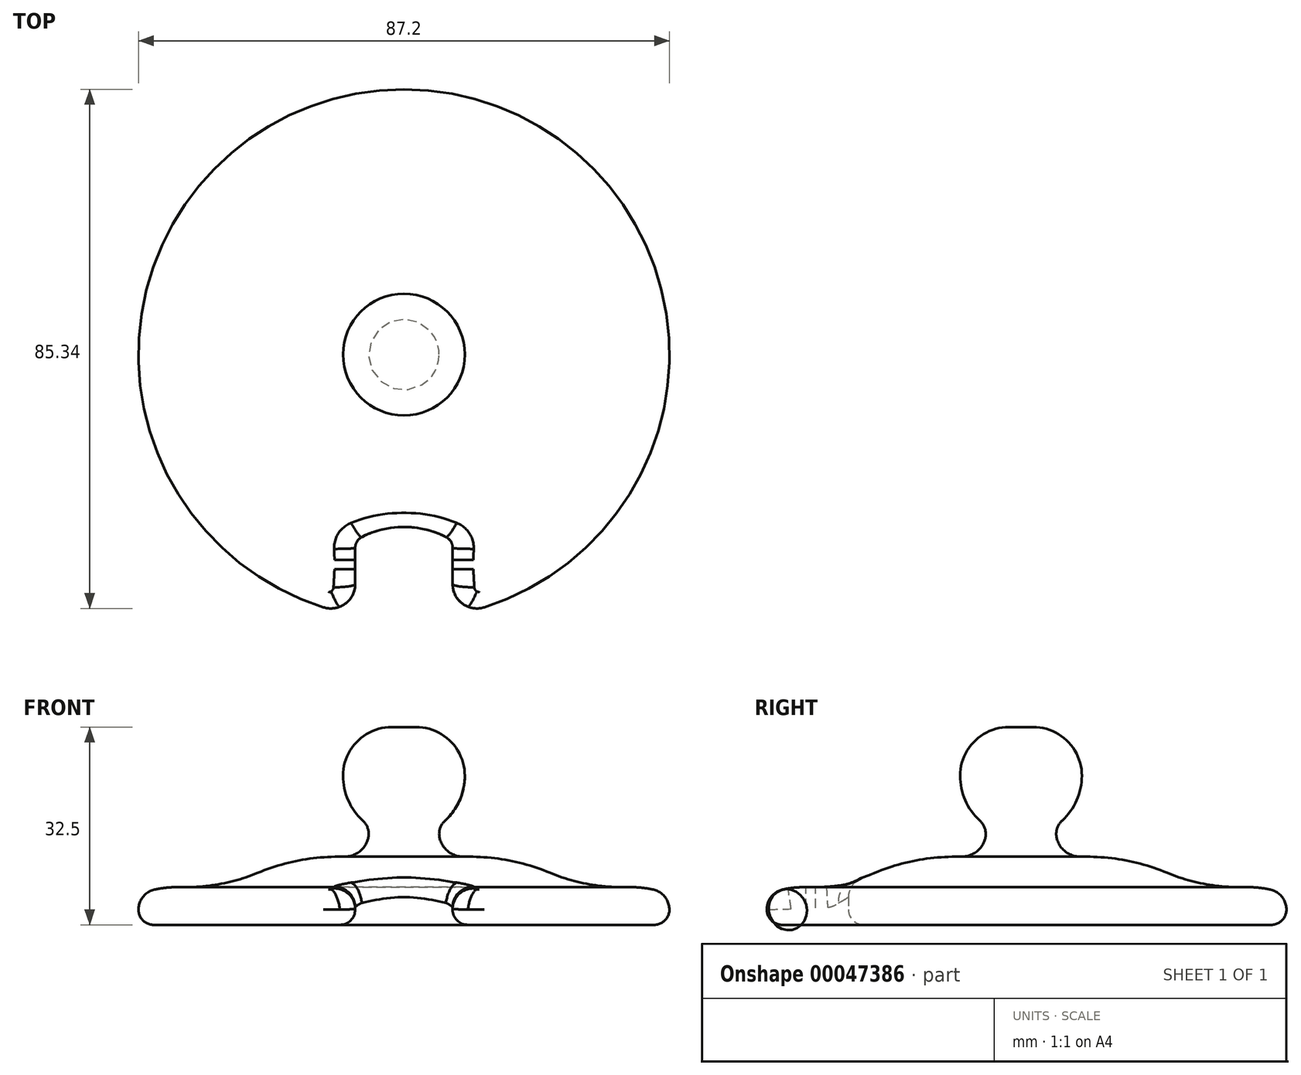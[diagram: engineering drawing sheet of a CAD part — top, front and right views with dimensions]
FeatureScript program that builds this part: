
annotation { "Feature Type Name" : "Feature", "Feature Type Description" : "" }
export const myFeature = defineFeature(function(context is Context, id is Id, definition is map)
    precondition{}
    {
        {
            var Q0;
            Q0=qCreatedBy(makeId("Front.planeOp"),FACE);
            var sketch = newSketch(context, id + "F0", { "sketchPlane" : qUnion([Q0])});
            skLineSegment(sketch, "E0", {"start": v(0, 0) * mm, "end": v(0, 28.7) * mm, "construction": true});
            skLineSegment(sketch, "E1", {"start": v(0, 0) * mm, "end": v(-41.1, 0) * mm});
            skLineSegment(sketch, "E2", {"start": v(-43.6, 2.5) * mm, "end": v(-43.6, 5) * mm});
            skLineSegment(sketch, "E3", {"start": v(-37.1, 6.2) * mm, "end": v(-28.6, 6.2) * mm});
            skLineSegment(sketch, "E4", {"start": v(-5.75, 11.2) * mm, "end": v(-10.75, 11.2) * mm});
            skLineSegment(sketch, "E5", {"start": v(-5.75, 11.2) * mm, "end": v(-5.75, 16.32) * mm});
            skArc(sketch, "E6", {"start": v(-6, 32.5) * mm, "mid": v(-9.49, 21.34) * mm, "end": v(0, 14.5) * mm});
            skPoint(sketch, "E7.visualSharp", {"position": v(-43.6, 0) * mm});
            skArc(sketch, "E7.filletArc", {"start": v(-43.6, 2.5) * mm, "mid": v(-42.87, 0.73) * mm, "end": v(-41.1, 0) * mm});
            skPoint(sketch, "E8.visualSharp", {"position": v(-43.6, 6.2) * mm});
            skArc(sketch, "E9", {"start": v(-10.75, 11.2) * mm, "mid": v(-20.02, 9.93) * mm, "end": v(-28.6, 6.2) * mm});
            skLineSegment(sketch, "E10", {"start": v(0, 32.5) * mm, "end": v(0, 0) * mm});
            skLineSegment(sketch, "E11", {"start": v(0, 32.5) * mm, "end": v(-6, 32.5) * mm});
            skPoint(sketch, "E12.orphan", {"position": v(0, 34.5) * mm});
            skArc(sketch, "E13", {"start": v(-37.1, 6.2) * mm, "mid": v(-40.4, 5.9) * mm, "end": v(-43.6, 5) * mm});
            skLineSegment(sketch, "E14", {"start": v(-43.6, 2.5) * mm, "end": v(-43.6, 0) * mm});
            skLineSegment(sketch, "E15", {"start": v(-41.1, 0) * mm, "end": v(-43.6, 0) * mm});
            skSolve(sketch);
        }
        {
            var Q0;
            Q0 = qSketchRegion(id + "F0", true);
            var Q1;
            Q1=sQuery(id+"F0.wireOp",EDGE,"E10");
            revolve(context, id + "F1", {"surfaceOperationType" : NewSurfaceOperationType.NEW, "entities" : qUnion([Q0]), "axis" : qUnion([Q1]), "revolveType" : RevolveType.FULL});
        }
        {
            var Q0;
            Q0=makeQuery(id+"F1.opRevolve","SWEPT_EDGE",EDGE,{"disambiguationData":[OSD([sQuery(id+"F0.wireOp",EDGE,"E3"),sQuery(id+"F0.wireOp",EDGE,"E9")])]});
            fillet(context, id + "F2", {"entities" : qUnion([Q0]), "radius" : 30 * mm, "tangentPropagation" : true, "allowEdgeOverflow" : false});
        }
        {
            var Q0;
            Q0=makeQuery(id+"F1.opRevolve","SWEPT_EDGE",EDGE,{"disambiguationData":[OSD([sQuery(id+"F0.wireOp",EDGE,"E4"),sQuery(id+"F0.wireOp",EDGE,"E5")])]});
            fillet(context, id + "F3", {"entities" : qUnion([Q0]), "radius" : 4 * mm, "tangentPropagation" : true, "allowEdgeOverflow" : false});
        }
        {
            var Q0;
            Q0=makeQuery(id+"F1.opRevolve","SWEPT_EDGE",EDGE,{"disambiguationData":[OSD([sQuery(id+"F0.wireOp",EDGE,"E5"),sQuery(id+"F0.wireOp",EDGE,"E6")])]});
            fillet(context, id + "F4", {"entities" : qUnion([Q0]), "radius" : 3 * mm, "tangentPropagation" : true, "allowEdgeOverflow" : false});
        }
        {
            var Q0;
            Q0=makeQuery(id+"F1.opRevolve","SWEPT_EDGE",EDGE,{"disambiguationData":[OSD([sQuery(id+"F0.wireOp",EDGE,"E6"),sQuery(id+"F0.wireOp",EDGE,"E11")])]});
            fillet(context, id + "F5", {"entities" : qUnion([Q0]), "radius" : 8 * mm, "tangentPropagation" : true, "allowEdgeOverflow" : false});
        }
        {
            var Q0;
            Q0=qCreatedBy(makeId("Top.planeOp"),FACE);
            var sketch = newSketch(context, id + "F6", { "sketchPlane" : qUnion([Q0])});
            skLineSegment(sketch, "E16.bottom", {"start": v(-8, -30.6) * mm, "end": v(8, -30.6) * mm});
            skLineSegment(sketch, "E16.top", {"start": v(-8, -43.6) * mm, "end": v(8, -43.6) * mm});
            skLineSegment(sketch, "E16.left", {"start": v(-8, -43.6) * mm, "end": v(-8, -30.6) * mm});
            skLineSegment(sketch, "E16.right", {"start": v(8, -43.6) * mm, "end": v(8, -30.6) * mm});
            skLineSegment(sketch, "E17", {"start": v(0, -43.6) * mm, "end": v(0, 0) * mm, "construction": true});
            skArc(sketch, "E18", {"start": v(8, -30.6) * mm, "mid": v(0, -28.34) * mm, "end": v(-8, -30.6) * mm});
            skSolve(sketch);
        }
        {
            var Q0;
            Q0 = qSketchRegion(id + "F6", true);
            extrude(context, id + "F7", {"entities" : qUnion([Q0]), "operationType" : NewBodyOperationType.REMOVE, "endBound" : BoundingType.THROUGH_ALL, "depth" : 25 * mm, "offsetDistance" : 25 * mm});
        }
        {
            var Q0;
            Q0=makeQuery(id+"F7.boolean.opBoolean","COPY",EDGE,{"derivedFrom":makeQuery(id+"F7.opExtrude","SWEPT_EDGE",EDGE,{"disambiguationData":[OSD([sQuery(id+"F6.wireOp",EDGE,"E16.bottom"),sQuery(id+"F6.wireOp",EDGE,"E16.left")])]})});
            var Q1;
            Q1=makeQuery(id+"F7.boolean.opBoolean","COPY",EDGE,{"derivedFrom":makeQuery(id+"F7.opExtrude","SWEPT_EDGE",EDGE,{"disambiguationData":[OSD([sQuery(id+"F6.wireOp",EDGE,"E16.bottom"),sQuery(id+"F6.wireOp",EDGE,"E16.right")])]})});
            fillet(context, id + "F8", {"entities" : qUnion([Q0, Q1]), "radius" : 2 * mm, "tangentPropagation" : true, "allowEdgeOverflow" : false});
        }
        {
            var Q0;
            Q0=makeQuery(id+"F7.boolean.opBoolean","INTERSECT",EDGE,{"derivedFrom":[makeQuery(id+"F1.opRevolve","SWEPT_FACE",FACE,{"disambiguationData":[OSD([sQuery(id+"F0.wireOp",EDGE,"E2"),sQuery(id+"F0.wireOp",EDGE,"E14")])]}),makeQuery(id+"F7.opExtrude","SWEPT_FACE",FACE,{"disambiguationData":[OSD([sQuery(id+"F6.wireOp",EDGE,"E16.left")])]})]});
            var Q1;
            Q1=makeQuery(id+"F7.boolean.opBoolean","INTERSECT",EDGE,{"derivedFrom":[makeQuery(id+"F1.opRevolve","SWEPT_FACE",FACE,{"disambiguationData":[OSD([sQuery(id+"F0.wireOp",EDGE,"E2"),sQuery(id+"F0.wireOp",EDGE,"E14")])]}),makeQuery(id+"F7.opExtrude","SWEPT_FACE",FACE,{"disambiguationData":[OSD([sQuery(id+"F6.wireOp",EDGE,"E16.right")])]})]});
            fillet(context, id + "F9", {"entities" : qUnion([Q0, Q1]), "radius" : 4 * mm, "tangentPropagation" : true, "allowEdgeOverflow" : false});
        }
        {
            var Q0;
            Q0=makeQuery(id+"F1.opRevolve","SWEPT_FACE",FACE,{"disambiguationData":[OSD([sQuery(id+"F0.wireOp",EDGE,"E1"),sQuery(id+"F0.wireOp",EDGE,"E15")])]});
            fillet(context, id + "F10", {"entities" : qUnion([Q0]), "radius" : 2.5 * mm, "tangentPropagation" : true, "allowEdgeOverflow" : false});
        }
        {
            var Q0;
            Q0=makeQuery(id+"F1.opRevolve","SWEPT_EDGE",EDGE,{"disambiguationData":[OSD([sQuery(id+"F0.wireOp",EDGE,"E2"),sQuery(id+"F0.wireOp",EDGE,"E13")])]});
            fillet(context, id + "F11", {"entities" : qUnion([Q0]), "radius" : 3.4 * mm, "tangentPropagation" : true, "allowEdgeOverflow" : false});
        }
    });
